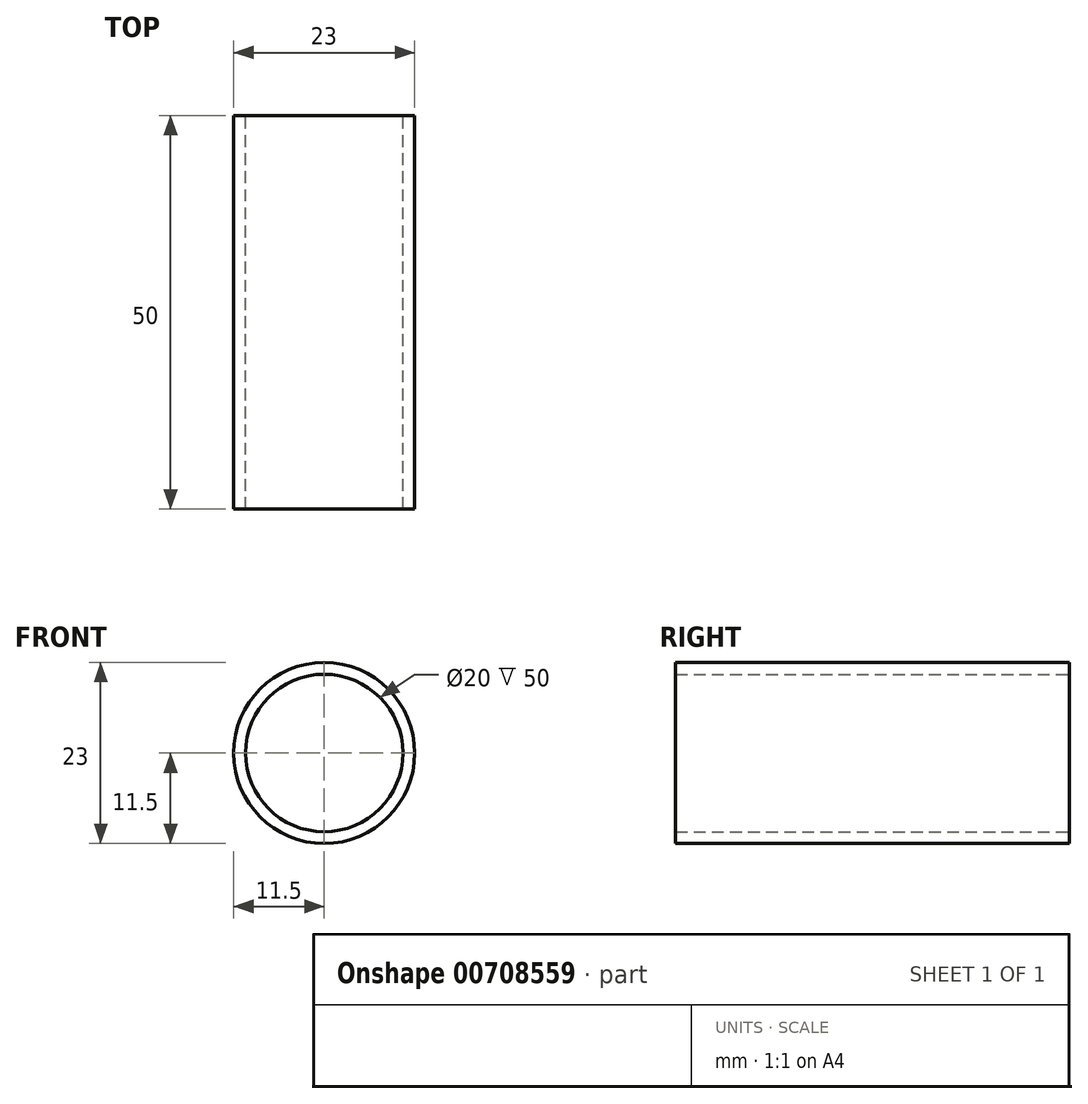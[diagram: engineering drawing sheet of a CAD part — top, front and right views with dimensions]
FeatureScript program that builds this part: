
annotation { "Feature Type Name" : "Feature", "Feature Type Description" : "" }
export const myFeature = defineFeature(function(context is Context, id is Id, definition is map)
    precondition{}
    {
        {
            var Q0;
            Q0=qCreatedBy(makeId("Front.planeOp"),FACE);
            var sketch = newSketch(context, id + "F0", { "sketchPlane" : qUnion([Q0])});
            skCircle(sketch, "E0", {"center": v(0, 0) * mm, "radius": 11.5 * mm});
            skCircle(sketch, "E1", {"center": v(0, 0) * mm, "radius": 10 * mm});
            skSolve(sketch);
        }
        {
            var Q0;
            Q0=makeQuery(id+"F0.imprint","IMPRINT",FACE,{"disambiguationData":[TD([[makeQuery(id+"F0.imprint","IMPRINT",EDGE,{"derivedFrom":sQuery(id+"F0.wireOp",EDGE,"E0")}),1.0]])]});
            extrude(context, id + "F1", {"entities" : qUnion([Q0]), "depth" : 50 * mm, "offsetDistance" : 25 * mm});
        }
    });
